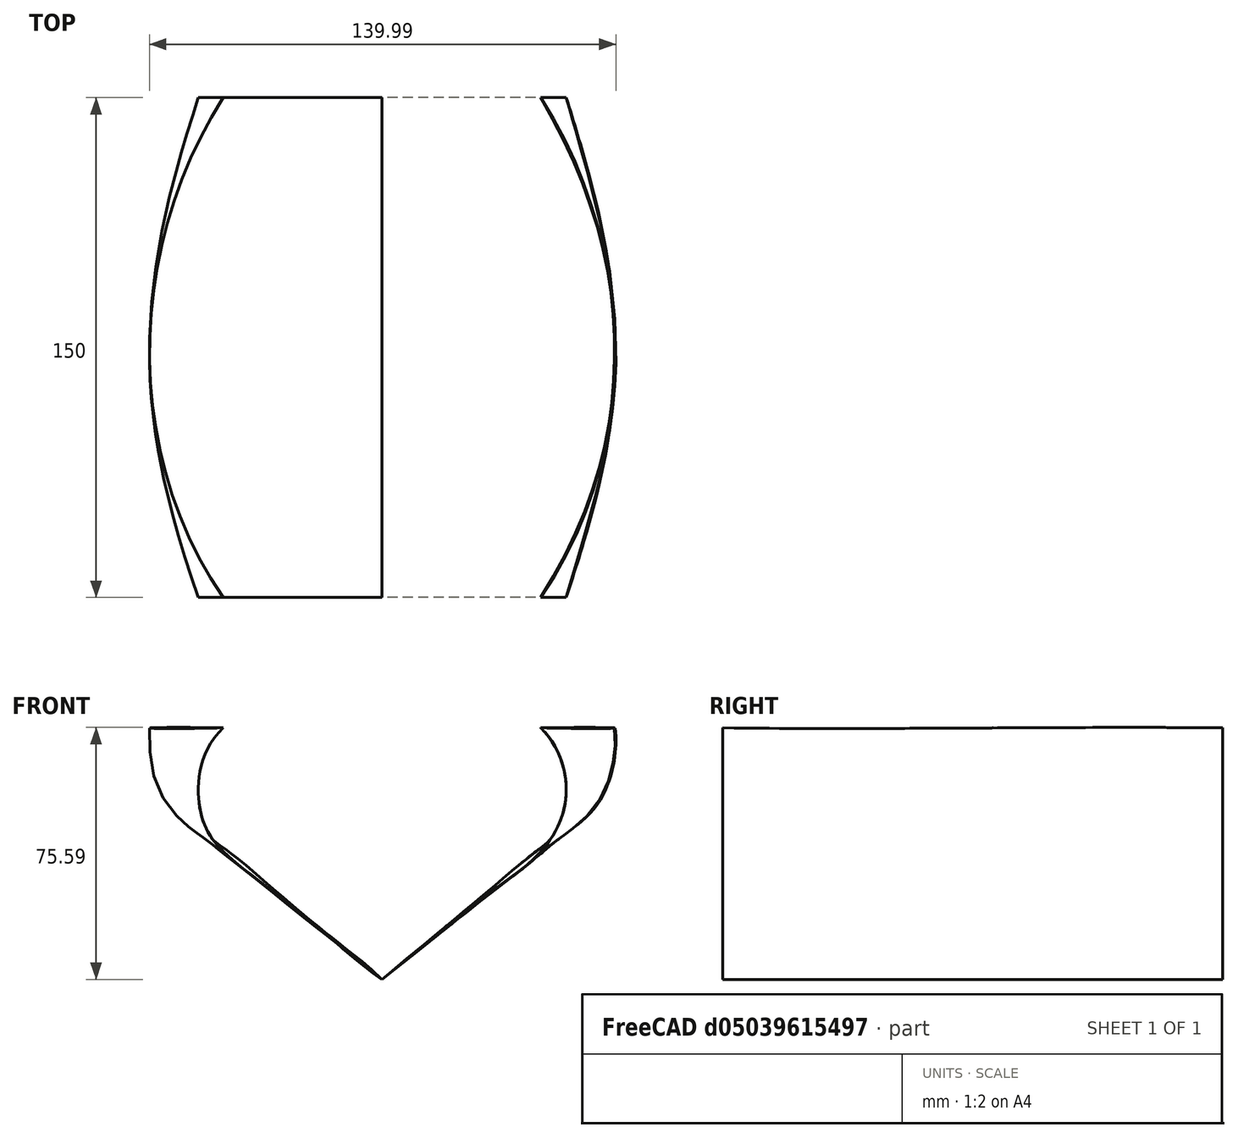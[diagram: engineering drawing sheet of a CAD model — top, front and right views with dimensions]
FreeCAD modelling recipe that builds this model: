
FCSTD DOCUMENT  (FreeCAD 0.21R33771 (Git))
Label: curves sample
License: All rights reserved
LicenseURL: http://en.wikipedia.org/wiki/All_rights_reserved
objects: Part::FeaturePython×12, Sketcher::SketchObject×4, App::DocumentObjectGroup×4, Part::Loft×2, Part::Mirroring×1
note: 19 computed .brp shape members not serialized (recipe doc carries the construction recipe); baked Part::Feature solids carry a one-line shape summary decoded from their .brp

FEATURE [Sketcher::SketchObject] Sketch
  FullyConstrained = false
  Placement = pos=(0,0,0) rot=(1,0,0;1.5708rad)
  sketch-geometry (15):
    g0: LineSegment StartX=0 StartY=15 StartZ=0 EndX=0 EndY=27.9369 EndZ=0
    g1: LineSegment StartX=0 StartY=27.9369 StartZ=0 EndX=0 EndY=40.8738 EndZ=0
    g2: LineSegment StartX=0 StartY=40.8738 StartZ=0 EndX=0 EndY=53.8106 EndZ=0
    g3: LineSegment StartX=0 StartY=53.8106 StartZ=0 EndX=0 EndY=66.7475 EndZ=0
    g4: LineSegment StartX=0 StartY=66.7475 StartZ=0 EndX=0 EndY=79.6844 EndZ=0
    g5: LineSegment StartX=0 StartY=0 StartZ=0 EndX=0 EndY=15 EndZ=0
    g6: LineSegment StartX=0 StartY=27.9369 StartZ=0 EndX=16.0152 EndY=27.9369 EndZ=0
    g7: LineSegment StartX=0 StartY=40.8738 StartZ=0 EndX=32.0305 EndY=40.8738 EndZ=0
    g8: LineSegment StartX=0 StartY=53.8106 StartZ=0 EndX=48.0457 EndY=53.8106 EndZ=0
    g9: LineSegment StartX=0 StartY=66.7475 StartZ=0 EndX=54.7423 EndY=66.7475 EndZ=0
    g10: LineSegment StartX=0 StartY=79.6844 StartZ=0 EndX=54.0807 EndY=79.6844 EndZ=0
    g11: LineSegment StartX=0 StartY=15 StartZ=0 EndX=48.0457 EndY=53.8106 EndZ=0
    g12: Circle CenterX=28.9201 CenterY=71.9123 CenterZ=0 NormalX=0 NormalY=0 NormalZ=1 AngleXU=0 Radius=26.3336
    g13: LineSegment StartX=0 StartY=79.6844 StartZ=0 EndX=0 EndY=90.4652 EndZ=0
    g14: LineSegment StartX=0 StartY=90.4652 StartZ=0 EndX=47.6082 EndY=90.4652 EndZ=0
  constraints (39):
    c: PointOnObject(g0,g-2)
    c: PointOnObject(g0,g-2)
    c: Coincident(g0,g1)
    c: PointOnObject(g1,g-2)
    c: Coincident(g1,g2)
    c: PointOnObject(g2,g-2)
    c: Coincident(g2,g3)
    c: PointOnObject(g3,g-2)
    c: Coincident(g3,g4)
    c: PointOnObject(g4,g-2)
    c: Equal(g4,g3)
    c: Equal(g3,g2)
    c: Equal(g2,g1)
    c: Equal(g1,g0)
    c: Coincident(g5,g-1)
    c: Coincident(g5,g0)
    c: Coincident(g6,g0)
    c: Horizontal(g6)
    c: Coincident(g7,g1)
    c: Horizontal(g7)
    c: Coincident(g8,g2)
    c: Horizontal(g8)
    c: Coincident(g9,g3)
    c: Horizontal(g9)
    c: Coincident(g10,g4)
    c: Horizontal(g10)
    c: DistanceY(g5,g5) = 15
    c: Coincident(g11,g0)
    c: PointOnObject(g6,g11)
    c: PointOnObject(g7,g11)
    c: Coincident(g11,g8)
    c: PointOnObject(g8,g12)
    c: PointOnObject(g9,g12)
    c: PointOnObject(g10,g12)
    c: Coincident(g4,g13)
    c: PointOnObject(g13,g-2)
    c: Coincident(g14,g13)
    c: PointOnObject(g14,g12)
    c: Horizontal(g14)
FEATURE [Part::FeaturePython] Interpolation_Curve  # WARN: FeaturePython — macro-defined, semantics opaque (R4)
  CustomTangents = false
  DetectAligned = false
  Parameters = [0,0.123451,0.250625,0.393641,0.59576,0.79788,1]
  Parametrization = 0
  Periodic = false
  PointList = -> [Sketch]
  Polygonal = false
  StartOffset = 0
  Tangents = (7) [(0.720954,1.53873e-16,-0.692983),(0.289527,2.12534e-16,-0.95717),(-0.204944,2.17331e-16,-0.978774),(-0.655596,1.67669e-16,-0.755112),+3 more]
  Tolerance = 1e-07
  UTurns = 0
  VTurns = 0
  WireOutput = false
FEATURE [App::DocumentObjectGroup] Group  label="Section1"
  Group = -> [Sketch,Interpolation_Curve]
FEATURE [Sketcher::SketchObject] Sketch001
  FullyConstrained = false
  Placement = pos=(0,50,0) rot=(1,0,0;1.5708rad)
  sketch-geometry (15):
    g0: LineSegment StartX=0 StartY=15 StartZ=0 EndX=0 EndY=27.9378 EndZ=0
    g1: LineSegment StartX=0 StartY=27.9378 StartZ=0 EndX=0 EndY=40.8755 EndZ=0
    g2: LineSegment StartX=0 StartY=40.8755 StartZ=0 EndX=0 EndY=53.8133 EndZ=0
    g3: LineSegment StartX=0 StartY=53.8133 StartZ=0 EndX=0 EndY=66.7511 EndZ=0
    g4: LineSegment StartX=0 StartY=66.7511 StartZ=0 EndX=0 EndY=79.6889 EndZ=0
    g5: LineSegment StartX=0 StartY=0 StartZ=0 EndX=0 EndY=15 EndZ=0
    g6: LineSegment StartX=0 StartY=27.9378 StartZ=0 EndX=15.6429 EndY=27.9378 EndZ=0
    g7: LineSegment StartX=0 StartY=40.8755 StartZ=0 EndX=31.2857 EndY=40.8755 EndZ=0
    g8: LineSegment StartX=0 StartY=53.8133 StartZ=0 EndX=46.9286 EndY=53.8133 EndZ=0
    g9: LineSegment StartX=0 StartY=66.7511 StartZ=0 EndX=62.8582 EndY=66.7511 EndZ=0
    g10: LineSegment StartX=0 StartY=79.6889 StartZ=0 EndX=67.8037 EndY=79.6889 EndZ=0
    g11: LineSegment StartX=0 StartY=15 StartZ=0 EndX=46.9286 EndY=53.8133 EndZ=0
    g12: Circle CenterX=34.9549 CenterY=84.8314 CenterZ=0 NormalX=0 NormalY=0 NormalZ=1 AngleXU=0 Radius=33.2489
    g13: LineSegment StartX=0 StartY=79.6889 StartZ=0 EndX=0 EndY=90.3087 EndZ=0
    g14: LineSegment StartX=0 StartY=90.3087 StartZ=0 EndX=67.7495 EndY=90.3087 EndZ=0
  constraints (39):
    c: PointOnObject(g0,g-2)
    c: PointOnObject(g0,g-2)
    c: Coincident(g0,g1)
    c: PointOnObject(g1,g-2)
    c: Coincident(g1,g2)
    c: PointOnObject(g2,g-2)
    c: Coincident(g2,g3)
    c: PointOnObject(g3,g-2)
    c: Coincident(g3,g4)
    c: PointOnObject(g4,g-2)
    c: Equal(g4,g3)
    c: Equal(g3,g2)
    c: Equal(g2,g1)
    c: Equal(g1,g0)
    c: Coincident(g5,g-1)
    c: Coincident(g5,g0)
    c: Coincident(g6,g0)
    c: Horizontal(g6)
    c: Coincident(g7,g1)
    c: Horizontal(g7)
    c: Coincident(g8,g2)
    c: Horizontal(g8)
    c: Coincident(g9,g3)
    c: Horizontal(g9)
    c: Coincident(g10,g4)
    c: Horizontal(g10)
    c: DistanceY(g5,g5) = 15
    c: Coincident(g11,g0)
    c: PointOnObject(g6,g11)
    c: PointOnObject(g7,g11)
    c: Coincident(g11,g8)
    c: PointOnObject(g8,g12)
    c: PointOnObject(g9,g12)
    c: PointOnObject(g10,g12)
    c: Coincident(g4,g13)
    c: PointOnObject(g13,g-2)
    c: Coincident(g14,g13)
    c: PointOnObject(g14,g12)
    c: Horizontal(g14)
FEATURE [Part::FeaturePython] Interpolation_Curve001  # WARN: FeaturePython — macro-defined, semantics opaque (R4)
  CustomTangents = false
  DetectAligned = false
  Parameters = [0,0.100291,0.231092,0.424889,0.616593,0.808296,1]
  Parametrization = 0
  Periodic = false
  PointList = -> [Sketch001]
  Polygonal = false
  StartOffset = 0
  Tangents = (7) [(0.720954,1.53873e-16,-0.692983),(0.289527,2.12534e-16,-0.95717),(-0.204944,2.17331e-16,-0.978774),(-0.655596,1.67669e-16,-0.755112),+3 more]
  Tolerance = 1e-07
  UTurns = 0
  VTurns = 0
  WireOutput = false
FEATURE [App::DocumentObjectGroup] Group001  label="Section002"
  Group = -> [Sketch001,Interpolation_Curve001]
FEATURE [Sketcher::SketchObject] Sketch002
  FullyConstrained = false
  Placement = pos=(0,100,0) rot=(1,0,0;1.5708rad)
  sketch-geometry (15):
    g0: LineSegment StartX=0 StartY=15 StartZ=0 EndX=0 EndY=27.9126 EndZ=0
    g1: LineSegment StartX=0 StartY=27.9126 StartZ=0 EndX=0 EndY=40.8252 EndZ=0
    g2: LineSegment StartX=0 StartY=40.8252 StartZ=0 EndX=0 EndY=53.7378 EndZ=0
    g3: LineSegment StartX=0 StartY=53.7378 StartZ=0 EndX=0 EndY=66.6504 EndZ=0
    g4: LineSegment StartX=0 StartY=66.6504 StartZ=0 EndX=0 EndY=79.563 EndZ=0
    g5: LineSegment StartX=0 StartY=0 StartZ=0 EndX=0 EndY=15 EndZ=0
    g6: LineSegment StartX=0 StartY=27.9126 StartZ=0 EndX=16.1185 EndY=27.9126 EndZ=0
    g7: LineSegment StartX=0 StartY=40.8252 StartZ=0 EndX=32.2369 EndY=40.8252 EndZ=0
    g8: LineSegment StartX=0 StartY=53.7378 StartZ=0 EndX=48.3554 EndY=53.7378 EndZ=0
    g9: LineSegment StartX=0 StartY=66.6504 StartZ=0 EndX=62.8858 EndY=66.6504 EndZ=0
    g10: LineSegment StartX=0 StartY=79.563 StartZ=0 EndX=67.5386 EndY=79.563 EndZ=0
    g11: LineSegment StartX=0 StartY=15 StartZ=0 EndX=48.3554 EndY=53.7378 EndZ=0
    g12: Circle CenterX=34.2224 CenterY=84.2734 CenterZ=0 NormalX=0 NormalY=0 NormalZ=1 AngleXU=0 Radius=33.6476
    g13: LineSegment StartX=0 StartY=79.563 StartZ=0 EndX=0 EndY=90.5432 EndZ=0
    g14: LineSegment StartX=0 StartY=90.5432 StartZ=0 EndX=67.2807 EndY=90.5432 EndZ=0
  constraints (39):
    c: PointOnObject(g0,g-2)
    c: PointOnObject(g0,g-2)
    c: Coincident(g0,g1)
    c: PointOnObject(g1,g-2)
    c: Coincident(g1,g2)
    c: PointOnObject(g2,g-2)
    c: Coincident(g2,g3)
    c: PointOnObject(g3,g-2)
    c: Coincident(g3,g4)
    c: PointOnObject(g4,g-2)
    c: Equal(g4,g3)
    c: Equal(g3,g2)
    c: Equal(g2,g1)
    c: Equal(g1,g0)
    c: Coincident(g5,g-1)
    c: Coincident(g5,g0)
    c: Coincident(g6,g0)
    c: Horizontal(g6)
    c: Coincident(g7,g1)
    c: Horizontal(g7)
    c: Coincident(g8,g2)
    c: Horizontal(g8)
    c: Coincident(g9,g3)
    c: Horizontal(g9)
    c: Coincident(g10,g4)
    c: Horizontal(g10)
    c: DistanceY(g5,g5) = 15
    c: Coincident(g11,g0)
    c: PointOnObject(g6,g11)
    c: PointOnObject(g7,g11)
    c: Coincident(g11,g8)
    c: PointOnObject(g8,g12)
    c: PointOnObject(g9,g12)
    c: PointOnObject(g10,g12)
    c: Coincident(g4,g13)
    c: PointOnObject(g13,g-2)
    c: Coincident(g14,g13)
    c: PointOnObject(g14,g12)
    c: Horizontal(g14)
FEATURE [Part::FeaturePython] Interpolation_Curve002  # WARN: FeaturePython — macro-defined, semantics opaque (R4)
  CustomTangents = false
  DetectAligned = false
  Parameters = [0,0.103511,0.232866,0.416069,0.610713,0.805356,1]
  Parametrization = 0
  Periodic = false
  PointList = -> [Sketch002]
  Polygonal = false
  StartOffset = 0
  Tangents = (7) [(0.720954,1.53873e-16,-0.692983),(0.289527,2.12534e-16,-0.95717),(-0.204944,2.17331e-16,-0.978774),(-0.655596,1.67669e-16,-0.755112),+3 more]
  Tolerance = 1e-07
  UTurns = 0
  VTurns = 0
  WireOutput = false
FEATURE [App::DocumentObjectGroup] Group002  label="Section003"
  Group = -> [Sketch002,Interpolation_Curve002]
FEATURE [Sketcher::SketchObject] Sketch003
  FullyConstrained = false
  Placement = pos=(0,150,0) rot=(1,0,0;1.5708rad)
  sketch-geometry (15):
    g0: LineSegment StartX=0 StartY=15 StartZ=0 EndX=0 EndY=27.9367 EndZ=0
    g1: LineSegment StartX=0 StartY=27.9367 StartZ=0 EndX=0 EndY=40.8733 EndZ=0
    g2: LineSegment StartX=0 StartY=40.8733 StartZ=0 EndX=0 EndY=53.81 EndZ=0
    g3: LineSegment StartX=0 StartY=53.81 StartZ=0 EndX=0 EndY=66.7467 EndZ=0
    g4: LineSegment StartX=0 StartY=66.7467 StartZ=0 EndX=0 EndY=79.6833 EndZ=0
    g5: LineSegment StartX=0 StartY=0 StartZ=0 EndX=0 EndY=15 EndZ=0
    g6: LineSegment StartX=0 StartY=27.9367 StartZ=0 EndX=16.0143 EndY=27.9367 EndZ=0
    g7: LineSegment StartX=0 StartY=40.8733 StartZ=0 EndX=32.0286 EndY=40.8733 EndZ=0
    g8: LineSegment StartX=0 StartY=53.81 StartZ=0 EndX=48.0429 EndY=53.81 EndZ=0
    g9: LineSegment StartX=0 StartY=66.7467 StartZ=0 EndX=54.7408 EndY=66.7467 EndZ=0
    g10: LineSegment StartX=0 StartY=79.6833 StartZ=0 EndX=54.0802 EndY=79.6833 EndZ=0
    g11: LineSegment StartX=0 StartY=15 StartZ=0 EndX=48.0429 EndY=53.81 EndZ=0
    g12: Circle CenterX=28.9192 CenterY=71.9134 CenterZ=0 NormalX=0 NormalY=0 NormalZ=1 AngleXU=0 Radius=26.3334
    g13: LineSegment StartX=0 StartY=79.6833 StartZ=0 EndX=0 EndY=90.4652 EndZ=0
    g14: LineSegment StartX=0 StartY=90.4652 StartZ=0 EndX=47.6082 EndY=90.4652 EndZ=0
  constraints (39):
    c: PointOnObject(g0,g-2)
    c: PointOnObject(g0,g-2)
    c: Coincident(g0,g1)
    c: PointOnObject(g1,g-2)
    c: Coincident(g1,g2)
    c: PointOnObject(g2,g-2)
    c: Coincident(g2,g3)
    c: PointOnObject(g3,g-2)
    c: Coincident(g3,g4)
    c: PointOnObject(g4,g-2)
    c: Equal(g4,g3)
    c: Equal(g3,g2)
    c: Equal(g2,g1)
    c: Equal(g1,g0)
    c: Coincident(g5,g-1)
    c: Coincident(g5,g0)
    c: Coincident(g6,g0)
    c: Horizontal(g6)
    c: Coincident(g7,g1)
    c: Horizontal(g7)
    c: Coincident(g8,g2)
    c: Horizontal(g8)
    c: Coincident(g9,g3)
    c: Horizontal(g9)
    c: Coincident(g10,g4)
    c: Horizontal(g10)
    c: DistanceY(g5,g5) = 15
    c: Coincident(g11,g0)
    c: PointOnObject(g6,g11)
    c: PointOnObject(g7,g11)
    c: Coincident(g11,g8)
    c: PointOnObject(g8,g12)
    c: PointOnObject(g9,g12)
    c: PointOnObject(g10,g12)
    c: Coincident(g4,g13)
    c: PointOnObject(g13,g-2)
    c: Coincident(g14,g13)
    c: PointOnObject(g14,g12)
    c: Horizontal(g14)
FEATURE [Part::FeaturePython] Interpolation_Curve003  # WARN: FeaturePython — macro-defined, semantics opaque (R4)
  CustomTangents = false
  DetectAligned = false
  Parameters = [0,0.12346,0.250634,0.393655,0.59577,0.797885,1]
  Parametrization = 0
  Periodic = false
  PointList = -> [Sketch003]
  Polygonal = false
  StartOffset = 0
  Tangents = (7) [(0.720954,1.53873e-16,-0.692983),(0.289527,2.12534e-16,-0.95717),(-0.204944,2.17331e-16,-0.978774),(-0.655596,1.67669e-16,-0.755112),+3 more]
  Tolerance = 1e-07
  UTurns = 0
  VTurns = 0
  WireOutput = false
FEATURE [App::DocumentObjectGroup] Group003  label="Section004"
  Group = -> [Sketch003,Interpolation_Curve003]
FEATURE [Part::FeaturePython] Interpolation_Curve004  # WARN: FeaturePython — macro-defined, semantics opaque (R4)
  CustomTangents = false
  DetectAligned = false
  Parameters = [0,0.341951,0.65915,1]
  Parametrization = 0
  Periodic = false
  PointList = -> [Sketch,Sketch001,Sketch002,Sketch003]
  Polygonal = false
  StartOffset = 0
  Tangents = (4) [(0,1,-8.52651e-16),(1.06581e-16,1,6.39488e-16),(1.26218e-31,1,-2.13163e-16),(6.31089e-32,1,2.52435e-31)]
  Tolerance = 1e-07
  UTurns = 0
  VTurns = 0
  WireOutput = false
FEATURE [Part::FeaturePython] Interpolation_Curve005  # WARN: FeaturePython — macro-defined, semantics opaque (R4)
  CustomTangents = false
  DetectAligned = false
  Parameters = [0,0.337494,0.662957,1]
  Parametrization = 0
  Periodic = false
  PointList = -> [Sketch,Sketch001,Sketch002,Sketch003]
  Polygonal = false
  StartOffset = 0
  Tangents = (4) [(0,1,0),(1.42109e-16,1,1.42109e-16),(-7.10543e-17,1,-7.10543e-17),(-1.26218e-31,1,-1.26218e-31)]
  Tolerance = 1e-07
  UTurns = 0
  VTurns = 0
  WireOutput = false
FEATURE [Part::FeaturePython] Interpolation_Curve006  # WARN: FeaturePython — macro-defined, semantics opaque (R4)
  CustomTangents = false
  DetectAligned = false
  Parameters = [0,0.334764,0.665204,1]
  Parametrization = 0
  Periodic = false
  PointList = -> [Sketch,Sketch001,Sketch002,Sketch003]
  Polygonal = false
  StartOffset = 0
  Tangents = (4) [(-4.26326e-16,1,0),(2.4869e-16,1,2.13163e-16),(-7.10543e-17,1,2.52435e-31),(-1.26218e-31,1,1.26218e-31)]
  Tolerance = 1e-07
  UTurns = 0
  VTurns = 0
  WireOutput = false
FEATURE [Part::FeaturePython] Interpolation_Curve007  # WARN: FeaturePython — macro-defined, semantics opaque (R4)
  CustomTangents = false
  DetectAligned = false
  Parameters = [0,0.333341,0.666735,1]
  Parametrization = 0
  Periodic = false
  PointList = -> [Sketch,Sketch001,Sketch002,Sketch003]
  Polygonal = false
  StartOffset = 0
  Tangents = (4) [(0,1,0),(1.06581e-16,1,1.42109e-16),(1.26218e-31,1,3.55271e-17),(6.31089e-32,1,-1.26218e-31)]
  Tolerance = 1e-07
  UTurns = 0
  VTurns = 0
  WireOutput = false
FEATURE [Part::FeaturePython] Interpolation_Curve008  # WARN: FeaturePython — macro-defined, semantics opaque (R4)
  CustomTangents = false
  DetectAligned = false
  Parameters = [0,0.333337,0.666697,1]
  Parametrization = 0
  Periodic = false
  PointList = -> [Sketch,Sketch001,Sketch002,Sketch003]
  Polygonal = false
  StartOffset = 0
  Tangents = (4) [(0,1,-4.26326e-16),(7.10543e-17,1,2.4869e-16),(-3.55271e-17,1,-7.10543e-17),(-6.31089e-32,1,-1.26218e-31)]
  Tolerance = 1e-07
  UTurns = 0
  VTurns = 0
  WireOutput = false
FEATURE [Part::FeaturePython] Interpolation_Curve009  # WARN: FeaturePython — macro-defined, semantics opaque (R4)
  CustomTangents = false
  DetectAligned = false
  Parameters = [0,0.333334,0.666674,1]
  Parametrization = 0
  Periodic = false
  PointList = -> [Sketch,Sketch001,Sketch002,Sketch003]
  Polygonal = false
  StartOffset = 0
  Tangents = (4) [(0,1,-2.13163e-16),(5.32907e-17,1,1.42109e-16),(6.31089e-32,1,-1.77636e-17),(3.15544e-32,1,-6.31089e-32)]
  Tolerance = 1e-07
  UTurns = 0
  VTurns = 0
  WireOutput = false
FEATURE [Part::FeaturePython] Interpolation_Curve010  # WARN: FeaturePython — macro-defined, semantics opaque (R4)
  CustomTangents = false
  DetectAligned = false
  Parameters = [0,0.333333,0.666667,1]
  Parametrization = 0
  Periodic = false
  PointList = -> [Sketch,Sketch001,Sketch002,Sketch003]
  Polygonal = false
  StartOffset = 0
  Tangents = (4) [(-1.10417e-43,1,-1.06581e-16),(-2.00759e-44,1,7.10543e-17),(1.00379e-44,1,-8.88178e-18),(-2.00759e-44,1,-3.15544e-32)]
  Tolerance = 1e-07
  UTurns = 0
  VTurns = 0
  WireOutput = false
FEATURE [Part::FeaturePython] Gordon  # WARN: FeaturePython — macro-defined, semantics opaque (R4)
  FlipNormal = false
  MaxCtrlPts = 80
  Output = 0
  SamplesU = 16
  SamplesV = 16
  Sources = -> [Interpolation_Curve003,Interpolation_Curve002,Interpolation_Curve001,Interpolation_Curve,Interpolation_Curve004,Interpolation_Curve005,Interpolation_Curve006,Interpolation_Curve007,Interpolation_Curve008,Interpolation_Curve009,Interpolation_Curve010]
  Tol2D = 1e-05
  Tol3D = 0.01
FEATURE [Part::Loft] Loft
  Closed = false
  MaxDegree = 5
  Ruled = false
  Sections = -> [Interpolation_Curve,Interpolation_Curve001,Interpolation_Curve002,Interpolation_Curve003]
  Solid = false
FEATURE [Part::Loft] Loft001
  Closed = false
  MaxDegree = 5
  Ruled = false
  Sections = -> [Interpolation_Curve004,Interpolation_Curve005,Interpolation_Curve006,Interpolation_Curve007,Interpolation_Curve008,Interpolation_Curve009,Interpolation_Curve010]
  Solid = false
FEATURE [Part::Mirroring] Part__Mirroring  label="Loft001 (Mirror #1)"
  Base = (0,0,0)
  Normal = (1,0,0)
  Source = -> Loft001
